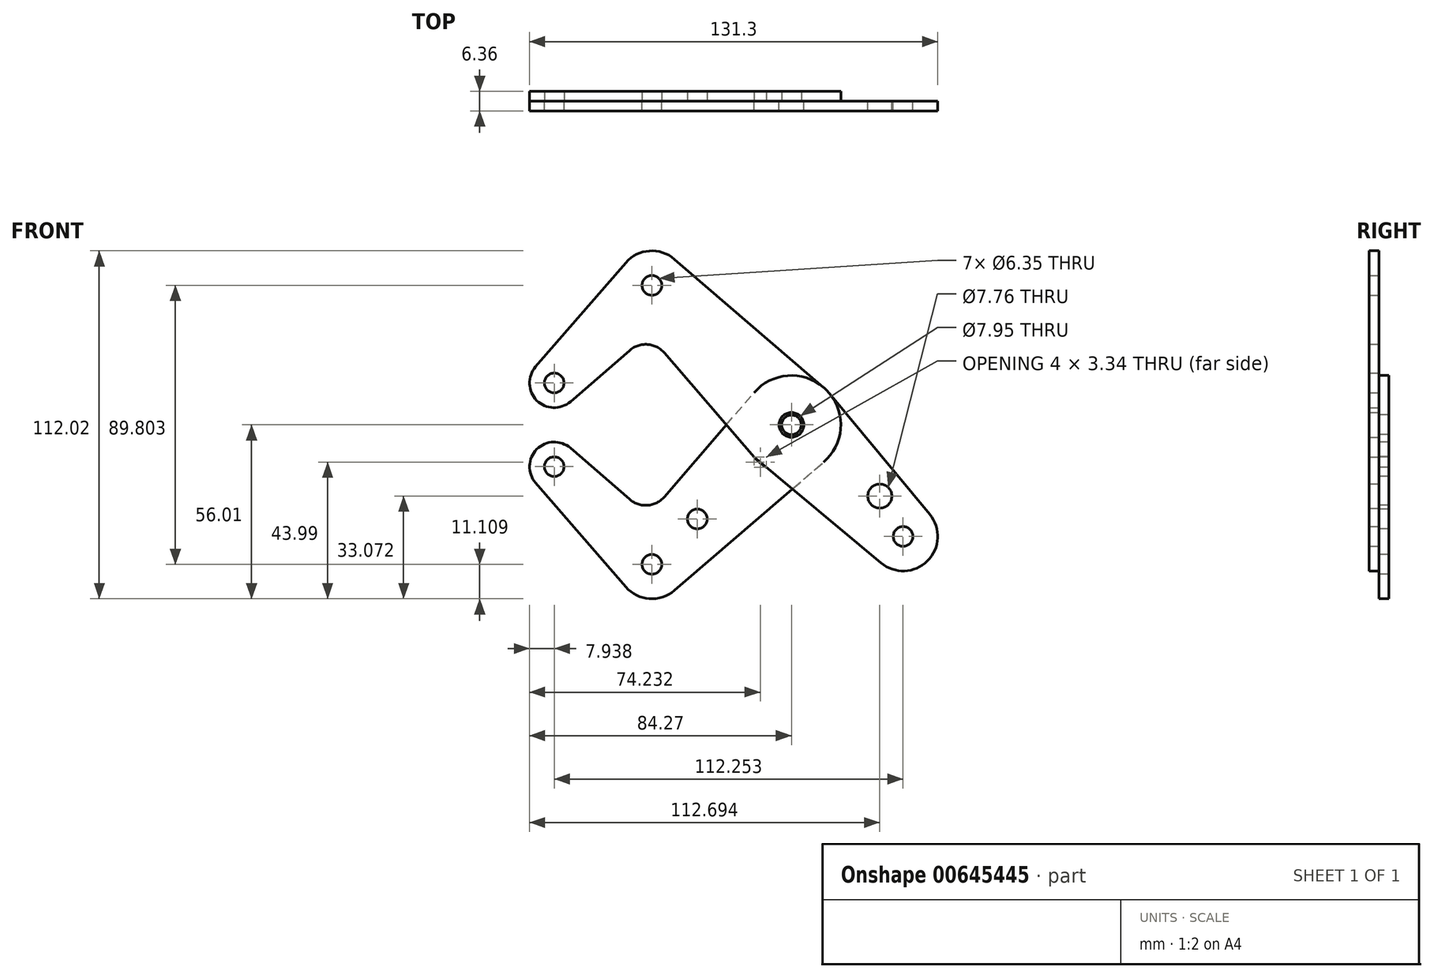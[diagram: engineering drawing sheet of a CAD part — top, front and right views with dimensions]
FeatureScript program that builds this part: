
annotation { "Feature Type Name" : "Feature", "Feature Type Description" : "" }
export const myFeature = defineFeature(function(context is Context, id is Id, definition is map)
    precondition{}
    {
        {
            var Q0;
            Q0=qCreatedBy(makeId("Front.planeOp"),FACE);
            var sketch = newSketch(context, id + "F0", { "sketchPlane" : qUnion([Q0])});
            skLineSegment(sketch, "E0", {"start": v(-76.33, 13.47) * mm, "end": v(-44.9, 44.9) * mm, "construction": true});
            skLineSegment(sketch, "E1", {"start": v(-44.9, 44.9) * mm, "end": v(35.92, -35.92) * mm, "construction": true});
            skCircle(sketch, "E2", {"center": v(-76.33, 13.47) * mm, "radius": 7.94 * mm});
            skCircle(sketch, "E3", {"center": v(0, 0) * mm, "radius": 15.88 * mm});
            skCircle(sketch, "E4", {"center": v(0, 0) * mm, "radius": 3.98 * mm});
            skCircle(sketch, "E5", {"center": v(35.92, -35.92) * mm, "radius": 11.11 * mm});
            skCircle(sketch, "E6", {"center": v(35.92, -35.92) * mm, "radius": 3.18 * mm});
            skCircle(sketch, "E7", {"center": v(0, 0) * mm, "radius": 3.18 * mm});
            skCircle(sketch, "E8", {"center": v(28.42, -22.94) * mm, "radius": 3.88 * mm});
            skCircle(sketch, "E9", {"center": v(-76.33, 13.47) * mm, "radius": 3.18 * mm});
            skCircle(sketch, "E10", {"center": v(-44.9, 44.9) * mm, "radius": 3.18 * mm});
            skCircle(sketch, "E11", {"center": v(-44.9, 44.9) * mm, "radius": 11.11 * mm});
            skLineSegment(sketch, "E12", {"start": v(-71.13, 7.47) * mm, "end": v(-52.08, 23.98) * mm});
            skLineSegment(sketch, "E13", {"start": v(-37.66, 53.33) * mm, "end": v(10.35, 12.04) * mm});
            skLineSegment(sketch, "E14", {"start": v(-40.85, 23.15) * mm, "end": v(-12.04, -10.35) * mm});
            skLineSegment(sketch, "E15", {"start": v(12.23, 10.12) * mm, "end": v(44.48, -28.83) * mm});
            skLineSegment(sketch, "E16", {"start": v(-12.04, -10.35) * mm, "end": v(28.8, -44.45) * mm});
            skLineSegment(sketch, "E17", {"start": v(-82.33, 18.67) * mm, "end": v(-53.3, 52.18) * mm});
            skArc(sketch, "E18.filletArc", {"start": v(-40.85, 23.15) * mm, "mid": v(-46.3, 25.9) * mm, "end": v(-52.08, 23.98) * mm});
            skLineSegment(sketch, "E19", {"start": v(0, 0) * mm, "end": v(-44.9, -44.9) * mm, "construction": true});
            skLineSegment(sketch, "E20", {"start": v(-44.9, -44.9) * mm, "end": v(-76.33, -13.47) * mm, "construction": true});
            skCircle(sketch, "E21", {"center": v(-76.33, -13.47) * mm, "radius": 7.94 * mm});
            skCircle(sketch, "E22", {"center": v(-76.33, -13.47) * mm, "radius": 3.18 * mm});
            skCircle(sketch, "E23", {"center": v(-44.9, -44.9) * mm, "radius": 11.11 * mm});
            skCircle(sketch, "E24", {"center": v(-44.9, -44.9) * mm, "radius": 3.18 * mm});
            skCircle(sketch, "E25", {"center": v(-30.3, -30.3) * mm, "radius": 3.18 * mm});
            skLineSegment(sketch, "E26", {"start": v(-82.33, -18.67) * mm, "end": v(-53.3, -52.18) * mm});
            skLineSegment(sketch, "E27", {"start": v(-37.66, -53.33) * mm, "end": v(11.26, -11.26) * mm});
            skLineSegment(sketch, "E28", {"start": v(-71.13, -7.47) * mm, "end": v(-52.08, -23.98) * mm});
            skLineSegment(sketch, "E29", {"start": v(-40.85, -23.15) * mm, "end": v(-11.26, 11.26) * mm});
            skArc(sketch, "E30.filletArc", {"start": v(-52.08, -23.98) * mm, "mid": v(-46.3, -25.9) * mm, "end": v(-40.85, -23.15) * mm});
            skSolve(sketch);
        }
        {
            var Q0;
            {var subQ0=sQuery(id+"F0.wireOp",EDGE,"E12");Q0=makeQuery(id+"F0.imprint","IMPRINT",FACE,{"disambiguationData":[TD([[makeQuery(id+"F0.imprint","IMPRINT",EDGE,{"derivedFrom":subQ0}),1.0]])]});}
            var Q1;
            Q1=makeQuery(id+"F0.imprint","IMPRINT",FACE,{"disambiguationData":[TD([[makeQuery(id+"F0.imprint","IMPRINT",EDGE,{"derivedFrom":sQuery(id+"F0.wireOp",EDGE,"E10")}),-1.0]])]});
            var Q2;
            Q2=makeQuery(id+"F0.imprint","IMPRINT",FACE,{"disambiguationData":[TD([[makeQuery(id+"F0.imprint","IMPRINT",EDGE,{"derivedFrom":sQuery(id+"F0.wireOp",EDGE,"E9")}),-1.0]])]});
            var Q3;
            Q3=makeQuery(id+"F0.imprint","IMPRINT",FACE,{"disambiguationData":[TD([[makeQuery(id+"F0.imprint","IMPRINT",EDGE,{"derivedFrom":sQuery(id+"F0.wireOp",EDGE,"E4")}),-1.0]])]});
            var Q4;
            Q4=makeQuery(id+"F0.imprint","IMPRINT",FACE,{"disambiguationData":[TD([[makeQuery(id+"F0.imprint","IMPRINT",EDGE,{"derivedFrom":sQuery(id+"F0.wireOp",EDGE,"E6")}),-1.0]])]});
            var Q5;
            {var subQ3=sQuery(id+"F0.wireOp",EDGE,"E8");Q5=makeQuery(id+"F0.imprint","IMPRINT",FACE,{"disambiguationData":[TD([[makeQuery(id+"F0.imprint","IMPRINT",EDGE,{"derivedFrom":subQ3}),-1.0]])]});}
            var Q6;
            {var subQ1=sQuery(id+"F0.wireOp",EDGE,"E3");var subQ3=sQuery(id+"F0.wireOp",EDGE,"E29");var subQ4=makeQuery(id+"F0.imprint","INTERSECT",VERTEX,{"derivedFrom":[subQ1,subQ3]});Q6=makeQuery(id+"F0.imprint","IMPRINT",FACE,{"disambiguationData":[TD([[makeQuery(id+"F0.imprint","IMPRINT",EDGE,{"disambiguationData":[TD([[subQ4,1.0]])],"derivedFrom":subQ3}),-1.0]])]});}
            var Q7;
            {var subQ0=sQuery(id+"F0.wireOp",EDGE,"E27");var subQ1=sQuery(id+"F0.wireOp",EDGE,"E3");var subQ2=makeQuery(id+"F0.imprint","INTERSECT",VERTEX,{"derivedFrom":[subQ1,subQ0]});Q7=makeQuery(id+"F0.imprint","IMPRINT",FACE,{"disambiguationData":[TD([[makeQuery(id+"F0.imprint","IMPRINT",EDGE,{"disambiguationData":[TD([[subQ2,1.0]])],"derivedFrom":subQ1}),-1.0]])]});}
            extrude(context, id + "F1", {"entities" : qUnion([Q0, Q1, Q2, Q3, Q4, Q5, Q6, Q7]), "depth" : 3.17 * mm, "offsetDistance" : 25.4 * mm});
        }
        {
            var Q0;
            Q0=makeQuery(id+"F0.imprint","IMPRINT",FACE,{"disambiguationData":[TD([[makeQuery(id+"F0.imprint","IMPRINT",EDGE,{"derivedFrom":sQuery(id+"F0.wireOp",EDGE,"E25")}),-1.0]])]});
            var Q1;
            Q1=makeQuery(id+"F0.imprint","IMPRINT",FACE,{"disambiguationData":[TD([[makeQuery(id+"F0.imprint","IMPRINT",EDGE,{"derivedFrom":sQuery(id+"F0.wireOp",EDGE,"E24")}),-1.0]])]});
            var Q2;
            Q2=makeQuery(id+"F0.imprint","IMPRINT",FACE,{"disambiguationData":[TD([[makeQuery(id+"F0.imprint","IMPRINT",EDGE,{"derivedFrom":sQuery(id+"F0.wireOp",EDGE,"E22")}),-1.0]])]});
            var Q3;
            {var subQ0=sQuery(id+"F0.wireOp",EDGE,"E27");var subQ1=sQuery(id+"F0.wireOp",EDGE,"E3");var subQ2=makeQuery(id+"F0.imprint","INTERSECT",VERTEX,{"derivedFrom":[subQ1,subQ0]});Q3=makeQuery(id+"F0.imprint","IMPRINT",FACE,{"disambiguationData":[TD([[makeQuery(id+"F0.imprint","IMPRINT",EDGE,{"disambiguationData":[TD([[subQ2,1.0]])],"derivedFrom":subQ1}),-1.0]])]});}
            var Q4;
            {var subQ1=sQuery(id+"F0.wireOp",EDGE,"E3");var subQ3=sQuery(id+"F0.wireOp",EDGE,"E29");var subQ4=makeQuery(id+"F0.imprint","INTERSECT",VERTEX,{"derivedFrom":[subQ1,subQ3]});Q4=makeQuery(id+"F0.imprint","IMPRINT",FACE,{"disambiguationData":[TD([[makeQuery(id+"F0.imprint","IMPRINT",EDGE,{"disambiguationData":[TD([[subQ4,1.0]])],"derivedFrom":subQ3}),-1.0]])]});}
            var Q5;
            Q5=makeQuery(id+"F0.imprint","IMPRINT",FACE,{"disambiguationData":[TD([[makeQuery(id+"F0.imprint","IMPRINT",EDGE,{"derivedFrom":sQuery(id+"F0.wireOp",EDGE,"E4")}),-1.0]])]});
            var Q6;
            Q6=makeQuery(id+"F0.imprint","IMPRINT",FACE,{"disambiguationData":[TD([[makeQuery(id+"F0.imprint","IMPRINT",EDGE,{"derivedFrom":sQuery(id+"F0.wireOp",EDGE,"E4")}),1.0]])]});
            extrude(context, id + "F2", {"entities" : qUnion([Q0, Q1, Q2, Q3, Q4, Q5, Q6]), "oppositeDirection" : true, "depth" : 3.17 * mm, "offsetDistance" : 25.4 * mm});
        }
    });
